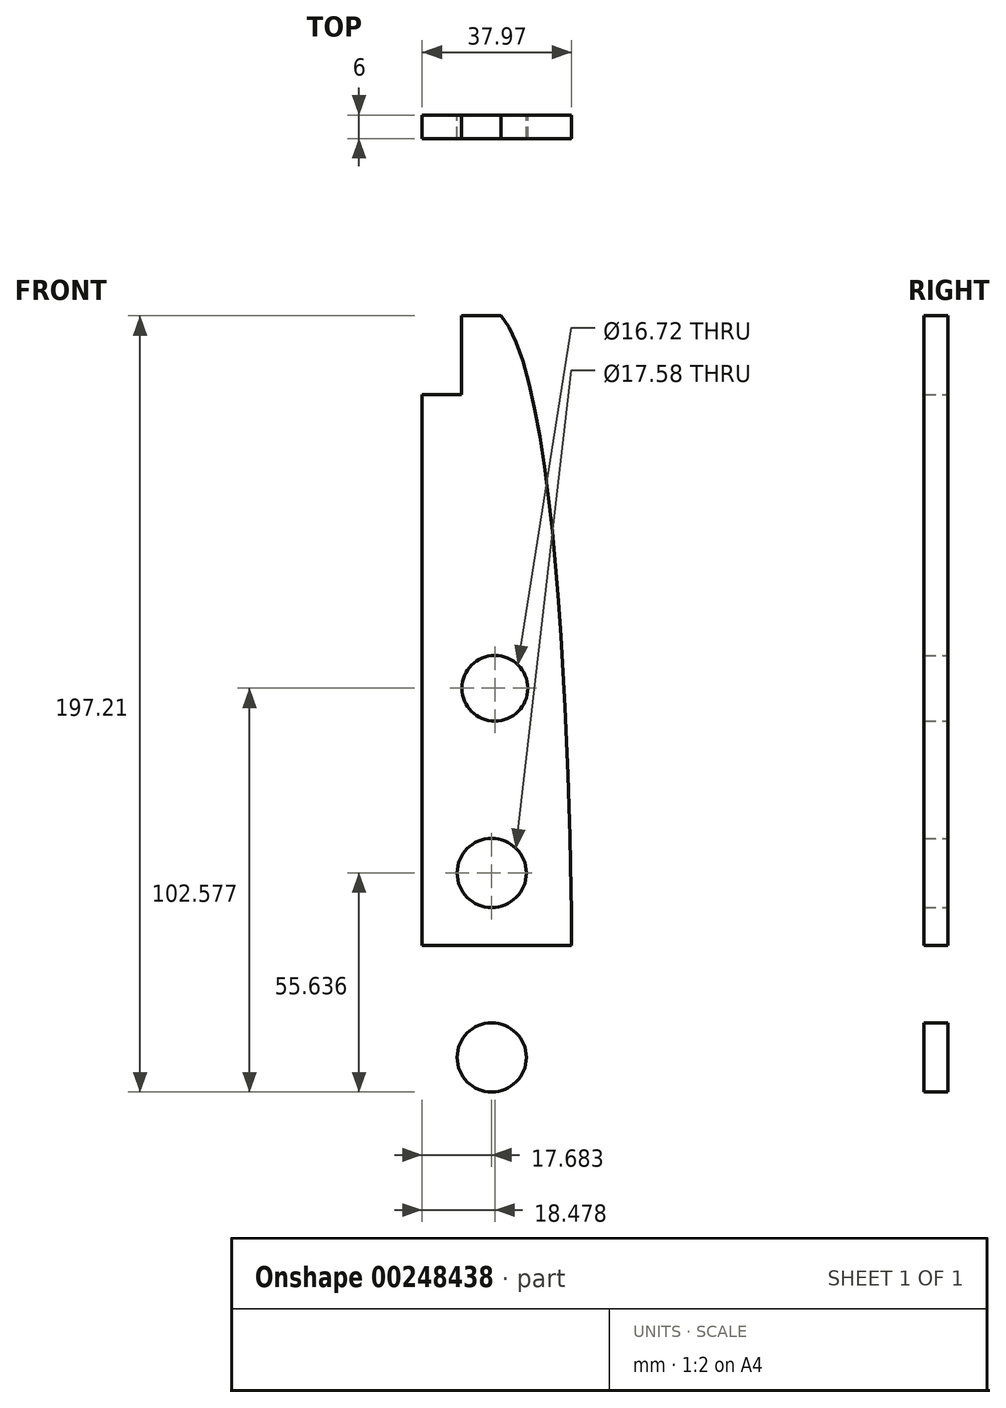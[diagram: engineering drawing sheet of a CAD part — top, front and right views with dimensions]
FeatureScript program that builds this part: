
annotation { "Feature Type Name" : "Feature", "Feature Type Description" : "" }
export const myFeature = defineFeature(function(context is Context, id is Id, definition is map)
    precondition{}
    {
        {
            var Q0;
            Q0=qCreatedBy(makeId("Front.planeOp"),FACE);
            var sketch = newSketch(context, id + "F0", { "sketchPlane" : qUnion([Q0])});
            skLineSegment(sketch, "E0.bottom", {"start": v(128.59, -74.96) * mm, "end": v(100.59, -74.96) * mm});
            skLineSegment(sketch, "E0.left", {"start": v(128.59, -74.96) * mm, "end": v(128.59, 255.04) * mm});
            skLineSegment(sketch, "E1", {"start": v(128.59, -74.96) * mm, "end": v(128.59, 90.04) * mm});
            skLineSegment(sketch, "E2", {"start": v(128.59, 90.04) * mm, "end": v(133.75, 90.04) * mm});
            skFitSpline(sketch, "E3", {"points": [v(110.59, 255.04) * mm, v(128.59, 90.04) * mm], "startDerivative": vector(54, -59.4) * mm, "endDerivative": vector(0, -5.5) * mm});
            skFitSpline(sketch, "E4.MirrorCS", {"points": [v(110.59, -74.96) * mm, v(128.59, 90.04) * mm], "startDerivative": vector(54, 59.4) * mm, "endDerivative": vector(0, 5.5) * mm});
            skLineSegment(sketch, "E5", {"start": v(93.09, 393.68) * mm, "end": v(92.01, 393.68) * mm});
            skLineSegment(sketch, "E6.MirrorCS", {"start": v(93.09, -213.6) * mm, "end": v(92.01, -213.6) * mm});
            skCircle(sketch, "E7", {"center": v(109.07, 160.4) * mm, "radius": 8.36 * mm});
            skCircle(sketch, "E8", {"center": v(108.27, 113.47) * mm, "radius": 8.8 * mm});
            skLineSegment(sketch, "E9", {"start": v(128.59, 90.04) * mm, "end": v(90.59, 90.04) * mm});
            skCircle(sketch, "E10.MirrorC", {"center": v(108.27, 66.62) * mm, "radius": 8.8 * mm});
            skCircle(sketch, "E11.MirrorC", {"center": v(109.07, 19.68) * mm, "radius": 8.36 * mm});
            skLineSegment(sketch, "E12", {"start": v(128.59, 90.04) * mm, "end": v(109.59, 90.04) * mm});
            skLineSegment(sketch, "E13", {"start": v(109.59, 90.04) * mm, "end": v(109.59, 85.04) * mm});
            skLineSegment(sketch, "E14", {"start": v(109.59, 90.04) * mm, "end": v(109.59, 95.04) * mm});
            skLineSegment(sketch, "E15", {"start": v(109.59, 95.04) * mm, "end": v(128.56, 95.04) * mm});
            skLineSegment(sketch, "E16", {"start": v(109.59, 85.04) * mm, "end": v(128.56, 85.04) * mm});
            skLineSegment(sketch, "E17", {"start": v(109.59, 95.04) * mm, "end": v(90.59, 95.04) * mm});
            skLineSegment(sketch, "E18", {"start": v(109.59, 85.04) * mm, "end": v(90.59, 85.04) * mm});
            skLineSegment(sketch, "E19", {"start": v(100.59, 255.04) * mm, "end": v(100.59, 235.04) * mm});
            skLineSegment(sketch, "E20", {"start": v(100.59, 235.04) * mm, "end": v(90.59, 235.04) * mm});
            skLineSegment(sketch, "E21", {"start": v(128.59, 255.04) * mm, "end": v(100.59, 255.04) * mm});
            skLineSegment(sketch, "E22.MirrorCS", {"start": v(100.59, -74.96) * mm, "end": v(100.59, -54.96) * mm});
            skLineSegment(sketch, "E23.MirrorCS", {"start": v(100.59, -54.96) * mm, "end": v(90.59, -54.96) * mm});
            skLineSegment(sketch, "E24", {"start": v(90.59, -54.96) * mm, "end": v(90.59, 235.04) * mm});
            skSolve(sketch);
        }
        {
            var Q0;
            {var subQ0=sQuery(id+"F0.wireOp",EDGE,"2aadc586-96c5-4e1f-9627-d2b55e743f49");Q0=makeQuery(id+"F0.imprint","IMPRINT",FACE,{"disambiguationData":[TD([[makeQuery(id+"F0.imprint","IMPRINT",EDGE,{"derivedFrom":subQ0}),-1.0]])]});}
            var Q1;
            Q1=makeQuery(id+"F0.imprint","IMPRINT",FACE,{"disambiguationData":[TD([[makeQuery(id+"F0.imprint","IMPRINT",EDGE,{"derivedFrom":sQuery(id+"F0.wireOp",EDGE,"E10.MirrorC")}),1.0]])]});
            var Q2;
            {var subQ0=sQuery(id+"F0.wireOp",EDGE,"E12");Q2=makeQuery(id+"F0.imprint","IMPRINT",FACE,{"disambiguationData":[TD([[makeQuery(id+"F0.imprint","IMPRINT",EDGE,{"derivedFrom":subQ0}),1.0]])]});}
            var Q3;
            {var subQ0=sQuery(id+"F0.wireOp",EDGE,"E12");Q3=makeQuery(id+"F0.imprint","IMPRINT",FACE,{"disambiguationData":[TD([[makeQuery(id+"F0.imprint","IMPRINT",EDGE,{"derivedFrom":subQ0}),-1.0]])]});}
            var Q4;
            Q4=makeQuery(id+"F0.imprint","IMPRINT",FACE,{"disambiguationData":[TD([[makeQuery(id+"F0.imprint","IMPRINT",EDGE,{"derivedFrom":sQuery(id+"F0.wireOp",EDGE,"E7")}),-1.0]])]});
            extrude(context, id + "F1", {"entities" : qUnion([Q0, Q1, Q2, Q3, Q4]), "depth" : 6 * mm});
        }
    });
